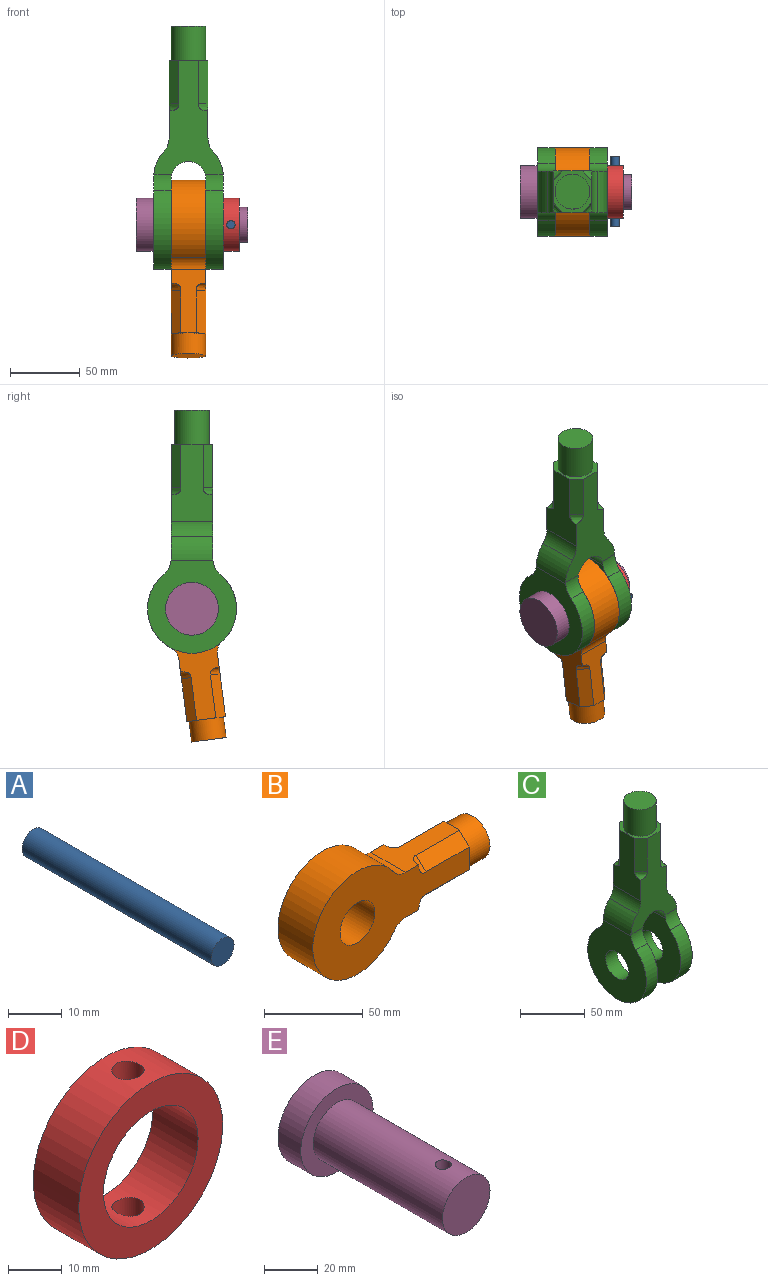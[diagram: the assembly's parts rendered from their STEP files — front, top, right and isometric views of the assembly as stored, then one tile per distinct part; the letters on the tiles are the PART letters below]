
ASSEMBLY  parts=5 mates=4
PART A: 3 faces, bbox 6x50x6 mm
  f0: cylinder r=3mm len=50mm, axis (0,1,0), area 942.5mm2, adj f1,f2
  f1: plane 6x6mm, normal (0,-1,0), area 28.3mm2, adj f0
  f2: plane 6x6mm, normal (0,1,0), area 28.3mm2, adj f0
PART B: 20 faces, bbox 129.2x35x66.2 mm
  f0: plane 47.72x27.19mm, normal (0,0,-1), area 646.9mm2, adj f2,f3,f7,f9,f12,f15,f18,f19
  f1: plane 25x14mm, normal (1,0,0), area 55.6mm2, adj f3,f4,f9,f10,f11,f13
  f2: plane 25x14mm, normal (1,0,0), area 55.6mm2, adj f0,f3,f9,f12,f13,f18
  f3: plane 114.19x66.19mm, normal (0,-1,0), area 3614.4mm2, adj f0,f1,f2,f4,f5,f6,f7,f8
  f4: plane 47.72x27.19mm, normal (0,0,1), area 646.9mm2, adj f1,f3,f5,f9,f10,f11,f16,f17
  f5: cylinder r=10mm len=25mm, axis (0,1,0), area 240.6mm2, adj f3,f4,f6,f9
  f6: cylinder r=32mm len=64mm, axis (0,1,0), area 4053.4mm2, adj f3,f5,f7,f9
  f7: cylinder r=10mm len=25mm, axis (0,1,0), area 240.6mm2, adj f0,f3,f6,f9
  f8: cylinder r=12.5mm len=25mm, axis (0,1,0), area 1963.5mm2, adj f3,f9
  f9: plane 114.19x66.19mm, normal (0,1,0), area 3614.4mm2, adj f0,f1,f2,f4,f5,f6,f7,f8
  f10: plane 31x7mm, normal (0,0.71,0.71), area 306.9mm2, adj f1,f4,f9,f17
  f11: plane 31x7mm, normal (0,-0.71,0.71), area 306.9mm2, adj f1,f3,f4,f16
  f12: plane 31x7mm, normal (0,-0.71,-0.71), area 306.9mm2, adj f0,f2,f3,f15
  f13: cylinder r=12.5mm len=25mm, axis (-1,0,0), area 1178.1mm2, adj f1,f2,f14
  f14: plane 25x25mm, normal (1,0,0), area 490.9mm2, adj f13
  f15: bspline ~11.24x11.24mm, area 40mm2, adj f0,f3,f12
  f16: bspline ~11.24x11.24mm, area 40mm2, adj f3,f4,f11
  f17: bspline ~11.24x11.24mm, area 40mm2, adj f4,f9,f10
  f18: plane 31x7mm, normal (0,0.71,-0.71), area 306.9mm2, adj f0,f2,f9,f19
  f19: bspline ~11.24x11.24mm, area 40mm2, adj f0,f9,f18
PART C: 32 faces, bbox 52.2x66.2x177.2 mm
  f0: plane 57.64x32.19mm, normal (-1,0,0), area 1170.5mm2, adj f1,f2,f8,f15,f23,f24,f26,f27
  f1: plane 30x28mm, normal (0,0,1), area 251.1mm2, adj f0,f2,f6,f15,f22,f23,f24,f25
  f2: plane 84x52.13mm, normal (0,-1,0), area 1938.3mm2, adj f0,f1,f6,f7,f8,f10,f11,f12
  f3: plane 67x64mm, normal (-1,0,0), area 2869.5mm2, adj f12,f13,f14,f18,f20
  f4: plane 65x64mm, normal (-1,0,0), area 2808.8mm2, adj f10,f16,f17,f19,f21
  f5: plane 65x64mm, normal (1,0,0), area 2808.8mm2, adj f10,f13,f14,f18,f20
  f6: plane 57.64x32.19mm, normal (1,0,0), area 1170.5mm2, adj f1,f2,f7,f15,f22,f25,f28,f29
  f7: cylinder r=15mm len=30mm, axis (0,-1,0), area 341.9mm2, adj f2,f6,f11,f15
  f8: cylinder r=15mm len=30mm, axis (0,-1,0), area 341.9mm2, adj f0,f2,f12,f15
  f9: plane 67x64mm, normal (1,0,0), area 2869.5mm2, adj f11,f16,f17,f19,f21
  f10: cylinder r=12.5mm len=30.68mm, axis (0,-1,0), area 1180.3mm2, adj f2,f4,f5,f14,f15,f16,f20,f21
  f11: cylinder r=25mm len=30.09mm, axis (0,-1,0), area 569.9mm2, adj f2,f7,f9,f15,f16,f21
  f12: cylinder r=25mm len=30.09mm, axis (0,-1,0), area 569.9mm2, adj f2,f3,f8,f14,f15,f20
  f13: cylinder r=32mm len=64mm, axis (1,0,0), area 1959.4mm2, adj f3,f5,f14,f20
  f14: cylinder r=15mm len=12.91mm, axis (1,0,0), area 165.4mm2, adj f3,f5,f10,f12,f13,f15
  f15: plane 84x52.13mm, normal (0,1,0), area 1938.3mm2, adj f0,f1,f6,f7,f8,f10,f11,f12
  f16: cylinder r=15mm len=12.91mm, axis (1,0,0), area 165.4mm2, adj f4,f9,f10,f11,f15,f17
  f17: cylinder r=32mm len=64mm, axis (1,0,0), area 1959.4mm2, adj f4,f9,f16,f21
  f18: cylinder r=12.5mm len=25mm, axis (1,0,0), area 981.7mm2, adj f3,f5
  f19: cylinder r=12.5mm len=25mm, axis (1,0,0), area 981.7mm2, adj f4,f9
  f20: cylinder r=15mm len=12.91mm, axis (1,0,0), area 165.4mm2, adj f2,f3,f5,f10,f12,f13
  f21: cylinder r=15mm len=12.91mm, axis (1,0,0), area 165.4mm2, adj f2,f4,f9,f10,f11,f17
  f22: plane 31x7mm, normal (0.71,-0.71,0), area 306.9mm2, adj f1,f2,f6,f28
  f23: plane 31x7mm, normal (-0.71,-0.71,0), area 306.9mm2, adj f0,f1,f2,f27
  f24: plane 31x7mm, normal (-0.71,0.71,0), area 306.9mm2, adj f0,f1,f15,f26
  f25: plane 31x7mm, normal (0.71,0.71,0), area 306.9mm2, adj f1,f6,f15,f29
  f26: bspline ~11.24x11.24mm, area 40mm2, adj f0,f15,f24
  f27: bspline ~11.24x11.24mm, area 40mm2, adj f0,f2,f23
  f28: bspline ~11.24x11.24mm, area 40mm2, adj f2,f6,f22
  f29: bspline ~11.24x11.24mm, area 40mm2, adj f6,f15,f25
  f30: cylinder r=12.5mm len=25mm, axis (0,0,-1), area 1963.5mm2, adj f1,f31
  f31: plane 25x25mm, normal (0,0,1), area 490.9mm2, adj f30
PART D: 6 faces, bbox 38x12x38 mm
  f0: cylinder r=12.5mm len=25mm, axis (0,1,0), area 885.6mm2, adj f2,f3,f4,f5
  f1: cylinder r=19mm len=38mm, axis (0,1,0), area 1376mm2, adj f2,f3,f4,f5
  f2: plane 38x38mm, normal (0,-1,0), area 643.2mm2, adj f0,f1
  f3: plane 38x38mm, normal (0,1,0), area 643.2mm2, adj f0,f1
  f4: cylinder r=3mm len=6.87mm, axis (0,0,1), area 123.7mm2, adj f0,f1
  f5: cylinder r=3mm len=6.87mm, axis (0,0,1), area 123.7mm2, adj f0,f1
PART E: 6 faces, bbox 38x80x38 mm
  f0: cylinder r=19mm len=38mm, axis (0,1,0), area 1432.6mm2, adj f1,f2
  f1: plane 38x38mm, normal (0,-1,0), area 643.2mm2, adj f0,f3
  f2: plane 38x38mm, normal (0,1,0), area 1134.1mm2, adj f0
  f3: cylinder r=12.5mm len=68mm, axis (0,1,0), area 5283.8mm2, adj f1,f4,f5
  f4: plane 25x25mm, normal (0,-1,0), area 490.9mm2, adj f3
  f5: cylinder r=3mm len=25mm, axis (0,0,1), area 464.4mm2, adj f3
PLACE A t=(30.38,37.31,-71.11)mm
PLACE B rot(axis=(-0.6,0.6,0.53),124.3deg) t=(-0.12,11.9,-71.11)mm
PLACE C t=(-0.12,11.9,-28.11)mm fixed
PLACE D rot(axis=(0.58,0.58,-0.58),120deg) t=(36.38,11.96,-71.11)mm
PLACE E rot(axis=(0.58,-0.58,0.58),120deg) t=(-31.62,11.9,-71.11)mm
MATE revolute B.f6 <-> C.f18  axis (-1,0,0) through (-12.62,11.9,-71.11)mm
MATE slider E.f3 <-> C.f18  axis (-1,0,0) through (8.38,11.9,-71.11)mm
MATE slider A.f0 <-> D.f4  axis (0,1,0) through (30.38,-12.69,-71.11)mm
MATE slider D.f4 <-> E.f5  axis (0,-1,0) through (30.38,-7.09,-71.11)mm
